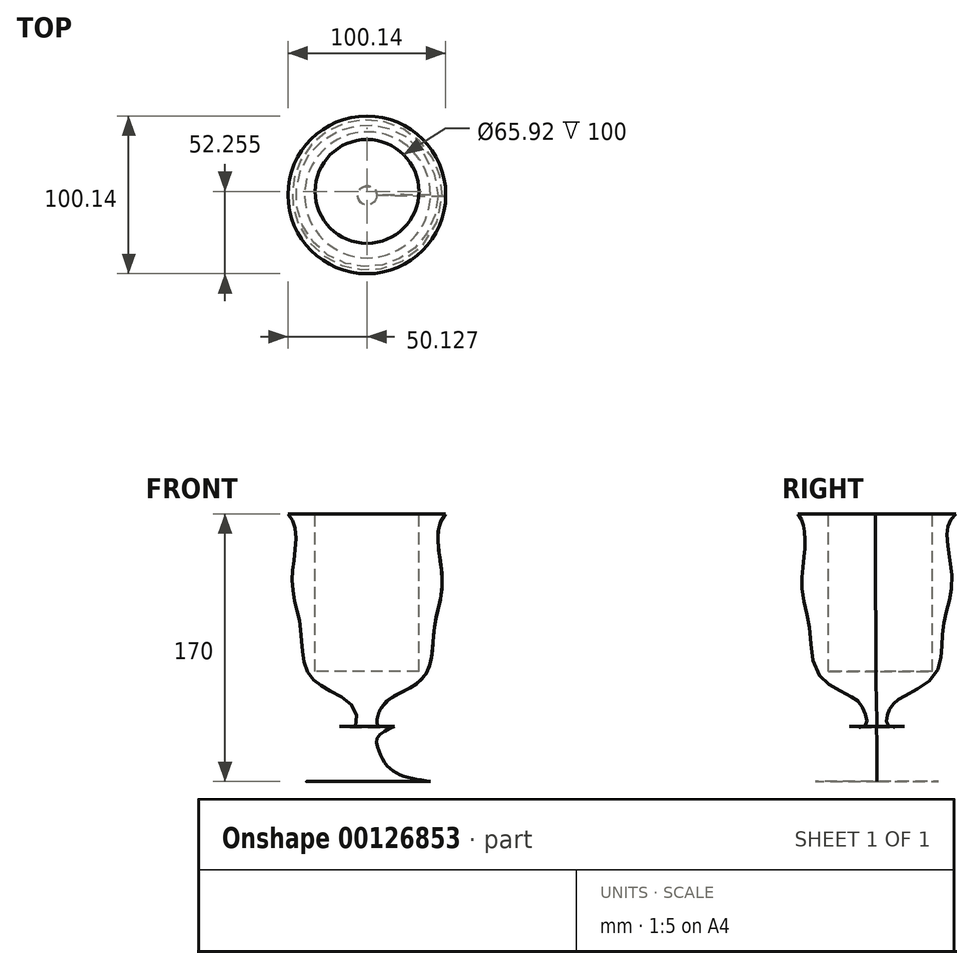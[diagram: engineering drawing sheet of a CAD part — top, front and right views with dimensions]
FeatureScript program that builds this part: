
annotation { "Feature Type Name" : "Feature", "Feature Type Description" : "" }
export const myFeature = defineFeature(function(context is Context, id is Id, definition is map)
    precondition{}
    {
        {
            var Q0;
            Q0=qCreatedBy(makeId("Top.planeOp"),FACE);
            cPlane(context, id + "F0", {"entities" : qUnion([Q0]), "cplaneType" : CPlaneType.OFFSET, "offset" : 10 * mm, "width" : 150 * mm, "height" : 150 * mm});
        }
        {
            var Q0;
            Q0=qCreatedBy(id+"F0.planeOp",FACE);
            cPlane(context, id + "F1", {"entities" : qUnion([Q0]), "cplaneType" : CPlaneType.OFFSET, "offset" : 2 * mm, "width" : 150 * mm, "height" : 150 * mm});
        }
        {
            var Q0;
            Q0=qCreatedBy(id+"F1.planeOp",FACE);
            cPlane(context, id + "F2", {"entities" : qUnion([Q0]), "cplaneType" : CPlaneType.OFFSET, "offset" : 7 * mm, "width" : 150 * mm, "height" : 150 * mm});
        }
        {
            var Q0;
            Q0=qCreatedBy(id+"F2.planeOp",FACE);
            cPlane(context, id + "F3", {"entities" : qUnion([Q0]), "cplaneType" : CPlaneType.OFFSET, "offset" : 10 * mm, "width" : 150 * mm, "height" : 150 * mm});
        }
        {
            var Q0;
            Q0=qCreatedBy(id+"F3.planeOp",FACE);
            cPlane(context, id + "F4", {"entities" : qUnion([Q0]), "cplaneType" : CPlaneType.OFFSET, "offset" : 6 * mm, "width" : 150 * mm, "height" : 150 * mm});
        }
        {
            var Q0;
            Q0=qCreatedBy(id+"F4.planeOp",FACE);
            cPlane(context, id + "F5", {"entities" : qUnion([Q0]), "cplaneType" : CPlaneType.OFFSET, "offset" : 2 * mm, "width" : 150 * mm, "height" : 150 * mm});
        }
        {
            var Q0;
            Q0=qCreatedBy(id+"F5.planeOp",FACE);
            cPlane(context, id + "F6", {"entities" : qUnion([Q0]), "cplaneType" : CPlaneType.OFFSET, "offset" : 7 * mm, "width" : 150 * mm, "height" : 150 * mm});
        }
        {
            var Q0;
            Q0=qCreatedBy(id+"F6.planeOp",FACE);
            cPlane(context, id + "F7", {"entities" : qUnion([Q0]), "cplaneType" : CPlaneType.OFFSET, "offset" : 4 * mm, "width" : 150 * mm, "height" : 150 * mm});
        }
        {
            var Q0;
            Q0=qCreatedBy(id+"F7.planeOp",FACE);
            cPlane(context, id + "F8", {"entities" : qUnion([Q0]), "cplaneType" : CPlaneType.OFFSET, "offset" : 10 * mm, "width" : 150 * mm, "height" : 150 * mm});
        }
        {
            var Q0;
            Q0=qCreatedBy(id+"F8.planeOp",FACE);
            cPlane(context, id + "F9", {"entities" : qUnion([Q0]), "cplaneType" : CPlaneType.OFFSET, "offset" : 10 * mm, "width" : 150 * mm, "height" : 150 * mm});
        }
        {
            var Q0;
            Q0=qCreatedBy(id+"F9.planeOp",FACE);
            cPlane(context, id + "F10", {"entities" : qUnion([Q0]), "cplaneType" : CPlaneType.OFFSET, "offset" : 30 * mm, "width" : 150 * mm, "height" : 150 * mm});
        }
        {
            var Q0;
            Q0=qCreatedBy(id+"F10.planeOp",FACE);
            cPlane(context, id + "F11", {"entities" : qUnion([Q0]), "cplaneType" : CPlaneType.OFFSET, "offset" : 25 * mm, "width" : 150 * mm, "height" : 150 * mm});
        }
        {
            var Q0;
            Q0=qCreatedBy(id+"F11.planeOp",FACE);
            cPlane(context, id + "F12", {"entities" : qUnion([Q0]), "cplaneType" : CPlaneType.OFFSET, "offset" : 25 * mm, "width" : 150 * mm, "height" : 150 * mm});
        }
        {
            var Q0;
            Q0=qCreatedBy(id+"F12.planeOp",FACE);
            cPlane(context, id + "F13", {"entities" : qUnion([Q0]), "cplaneType" : CPlaneType.OFFSET, "offset" : 20 * mm, "width" : 150 * mm, "height" : 150 * mm});
        }
        {
            var Q0;
            Q0=qCreatedBy(id+"F13.planeOp",FACE);
            cPlane(context, id + "F14", {"entities" : qUnion([Q0]), "cplaneType" : CPlaneType.OFFSET, "offset" : 2 * mm, "width" : 150 * mm, "height" : 150 * mm});
        }
        {
            var Q0;
            Q0=qCreatedBy(makeId("Top.planeOp"),FACE);
            var sketch = newSketch(context, id + "F15", { "sketchPlane" : qUnion([Q0])});
            skCircle(sketch, "E0", {"center": v(0.1, 0.56) * mm, "radius": 40 * mm});
            skSolve(sketch);
        }
        {
            var Q0;
            Q0=qCreatedBy(id+"F0.planeOp",FACE);
            var sketch = newSketch(context, id + "F16", { "sketchPlane" : qUnion([Q0])});
            skCircle(sketch, "E1", {"center": v(0, 0.58) * mm, "radius": 12.5 * mm});
            skSolve(sketch);
        }
        {
            var Q0;
            Q0=qCreatedBy(id+"F2.planeOp",FACE);
            var sketch = newSketch(context, id + "F17", { "sketchPlane" : qUnion([Q0])});
            skCircle(sketch, "E2", {"center": v(0, 0.29) * mm, "radius": 7.5 * mm});
            skSolve(sketch);
        }
        {
            var Q0;
            Q0=qCreatedBy(id+"F3.planeOp",FACE);
            var sketch = newSketch(context, id + "F18", { "sketchPlane" : qUnion([Q0])});
            skCircle(sketch, "E3", {"center": v(-0.29, 0) * mm, "radius": 7.5 * mm});
            skSolve(sketch);
        }
        {
            var Q0;
            Q0=qCreatedBy(id+"F4.planeOp",FACE);
            var sketch = newSketch(context, id + "F19", { "sketchPlane" : qUnion([Q0])});
            skCircle(sketch, "E4", {"center": v(-0.29, 0.58) * mm, "radius": 17.5 * mm});
            skSolve(sketch);
        }
        {
            var Q0;
            Q0=qCreatedBy(id+"F4.planeOp",FACE);
            var sketch = newSketch(context, id + "F20", { "sketchPlane" : qUnion([Q0])});
            skCircle(sketch, "E5", {"center": v(0, 0.58) * mm, "radius": 7.5 * mm});
            skSolve(sketch);
        }
        {
            var Q0;
            Q0=qCreatedBy(id+"F6.planeOp",FACE);
            var sketch = newSketch(context, id + "F21", { "sketchPlane" : qUnion([Q0])});
            skCircle(sketch, "E6", {"center": v(0, 0.29) * mm, "radius": 7.5 * mm});
            skSolve(sketch);
        }
        {
            var Q0;
            Q0=qCreatedBy(id+"F7.planeOp",FACE);
            var sketch = newSketch(context, id + "F22", { "sketchPlane" : qUnion([Q0])});
            skCircle(sketch, "E7", {"center": v(0, 0.58) * mm, "radius": 9.5 * mm});
            skSolve(sketch);
        }
        {
            var Q0;
            Q0=qCreatedBy(id+"F8.planeOp",FACE);
            var sketch = newSketch(context, id + "F23", { "sketchPlane" : qUnion([Q0])});
            skCircle(sketch, "E8", {"center": v(0, 0.58) * mm, "radius": 24.5 * mm});
            skSolve(sketch);
        }
        {
            var Q0;
            Q0=qCreatedBy(id+"F9.planeOp",FACE);
            var sketch = newSketch(context, id + "F24", { "sketchPlane" : qUnion([Q0])});
            skCircle(sketch, "E9", {"center": v(0, 0.58) * mm, "radius": 37 * mm});
            skSolve(sketch);
        }
        {
            var Q0;
            Q0=qCreatedBy(id+"F10.planeOp",FACE);
            var sketch = newSketch(context, id + "F25", { "sketchPlane" : qUnion([Q0])});
            skCircle(sketch, "E10", {"center": v(0, 0.29) * mm, "radius": 42.5 * mm});
            skSolve(sketch);
        }
        {
            var Q0;
            Q0=qCreatedBy(id+"F11.planeOp",FACE);
            var sketch = newSketch(context, id + "F26", { "sketchPlane" : qUnion([Q0])});
            skCircle(sketch, "E11", {"center": v(0, 0.58) * mm, "radius": 47.5 * mm});
            skSolve(sketch);
        }
        {
            var Q0;
            Q0=qCreatedBy(id+"F12.planeOp",FACE);
            var sketch = newSketch(context, id + "F27", { "sketchPlane" : qUnion([Q0])});
            skCircle(sketch, "E12", {"center": v(-0.29, 0.29) * mm, "radius": 45.5 * mm});
            skSolve(sketch);
        }
        {
            var Q0;
            Q0=qCreatedBy(id+"F13.planeOp",FACE);
            var sketch = newSketch(context, id + "F28", { "sketchPlane" : qUnion([Q0])});
            skCircle(sketch, "E13", {"center": v(-0.29, 0.29) * mm, "radius": 48.5 * mm});
            skSolve(sketch);
        }
        {
            var Q0;
            Q0=qCreatedBy(id+"F14.planeOp",FACE);
            var sketch = newSketch(context, id + "F29", { "sketchPlane" : qUnion([Q0])});
            skCircle(sketch, "E14", {"center": v(-0.29, 0.58) * mm, "radius": 50.07 * mm});
            skSolve(sketch);
        }
        {
            var Q0;
            Q0 = qSketchRegion(id + "F15", true);
            var Q1;
            Q1 = qSketchRegion(id + "F16", true);
            var Q2;
            Q2 = qSketchRegion(id + "F17", true);
            var Q3;
            Q3 = qSketchRegion(id + "F18", true);
            var Q4;
            Q4 = qSketchRegion(id + "F19", true);
            var Q5;
            Q5 = qSketchRegion(id + "F20", true);
            var Q6;
            Q6 = qSketchRegion(id + "F21", true);
            var Q7;
            Q7 = qSketchRegion(id + "F22", true);
            var Q8;
            Q8 = qSketchRegion(id + "F23", true);
            var Q9;
            Q9 = qSketchRegion(id + "F24", true);
            var Q10;
            Q10 = qSketchRegion(id + "F25", true);
            var Q11;
            Q11 = qSketchRegion(id + "F26", true);
            var Q12;
            Q12 = qSketchRegion(id + "F27", true);
            var Q13;
            Q13 = qSketchRegion(id + "F28", true);
            var Q14;
            Q14 = qSketchRegion(id + "F29", true);
            loft(context, id + "F30", {"sheetProfilesArray" : [{ "sheetProfileEntities" : qUnion([Q0]) }, { "sheetProfileEntities" : qUnion([Q1]) }, { "sheetProfileEntities" : qUnion([Q2]) }, { "sheetProfileEntities" : qUnion([Q3]) }, { "sheetProfileEntities" : qUnion([Q4]) }, { "sheetProfileEntities" : qUnion([Q5]) }, { "sheetProfileEntities" : qUnion([Q6]) }, { "sheetProfileEntities" : qUnion([Q7]) }, { "sheetProfileEntities" : qUnion([Q8]) }, { "sheetProfileEntities" : qUnion([Q9]) }, { "sheetProfileEntities" : qUnion([Q10]) }, { "sheetProfileEntities" : qUnion([Q11]) }, { "sheetProfileEntities" : qUnion([Q12]) }, { "sheetProfileEntities" : qUnion([Q13]) }, { "sheetProfileEntities" : qUnion([Q14]) }]});
        }
        {
            var Q0;
            Q0=makeQuery(id+"F30.opLoft","CAP_FACE",FACE,{"disambiguationData":[OSD([makeQuery(id+"F29.imprint","IMPRINT",FACE,{"disambiguationData":[TD([[makeQuery(id+"F29.imprint","IMPRINT",EDGE,{"derivedFrom":sQuery(id+"F29.wireOp",EDGE,"E14")}),1.0]])]})])],"isStart":true});
            var sketch = newSketch(context, id + "F31", { "sketchPlane" : qUnion([Q0])});
            skCircle(sketch, "E15", {"center": v(-0.23, 2.76) * mm, "radius": 32.96 * mm});
            skSolve(sketch);
        }
        {
            var Q0;
            Q0 = qSketchRegion(id + "F31", true);
            extrude(context, id + "F32", {"entities" : qUnion([Q0]), "operationType" : NewBodyOperationType.REMOVE, "oppositeDirection" : true, "depth" : 100 * mm});
        }
    });
